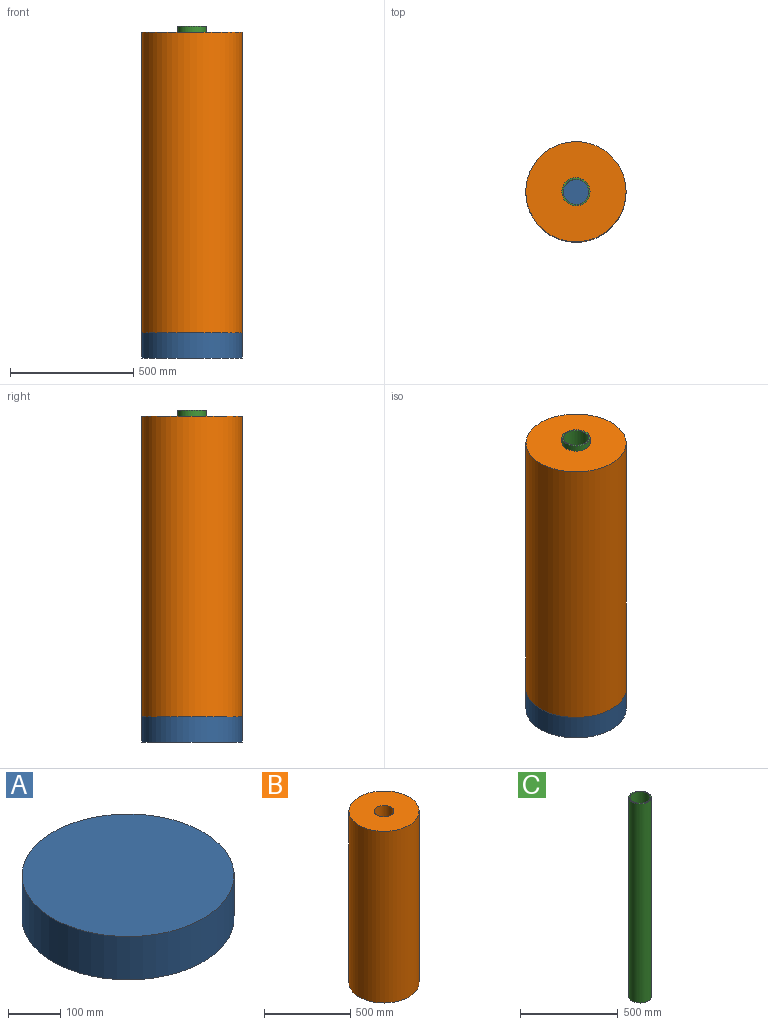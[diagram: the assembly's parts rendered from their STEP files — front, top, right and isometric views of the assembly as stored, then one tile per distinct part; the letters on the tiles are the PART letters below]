
ASSEMBLY  parts=3 mates=3
PART A: 3 faces, bbox 406.4x406.4x101.6 mm
  f0: cylinder r=203.2mm len=406.4mm, axis (0,0,-1), area 129717.1mm2, adj f1,f2
  f1: plane 406.4x406.4mm, normal (0,0,1), area 129717.1mm2, adj f0
  f2: plane 406.4x406.4mm, normal (0,0,-1), area 129717.1mm2, adj f0
PART B: 4 faces, bbox 406.4x406.4x1219.2 mm
  f0: cylinder r=57.15mm len=1219.2mm, axis (0,0,-1), area 437795.3mm2, adj f2,f3
  f1: cylinder r=203.2mm len=1219.2mm, axis (0,0,-1), area 1556605.4mm2, adj f2,f3
  f2: plane 406.4x406.4mm, normal (0,0,1), area 119456.3mm2, adj f0,f1
  f3: plane 406.4x406.4mm, normal (0,0,-1), area 119456.3mm2, adj f0,f1
PART C: 4 faces, bbox 114.3x114.3x1244.6 mm
  f0: cylinder r=51.18mm len=1244.6mm, axis (0,0,-1), area 400238.1mm2, adj f2,f3
  f1: cylinder r=57.15mm len=1244.6mm, axis (0,0,-1), area 446916mm2, adj f2,f3
  f2: plane 114.3x114.3mm, normal (0,0,1), area 2031.4mm2, adj f0,f1
  f3: plane 114.3x114.3mm, normal (0,0,-1), area 2031.4mm2, adj f0,f1
PLACE A t=(-13.41,3.24,-34.34)mm fixed
PLACE B t=(-13.41,3.24,67.26)mm
PLACE C t=(-13.41,3.24,67.26)mm
MATE fastened A.f0 <-> C.f1  axis (0,0,1) through (-13.41,3.24,67.26)mm
MATE fastened C.f1 <-> A.f0  axis (0,0,-1) through (-13.41,3.24,67.26)mm
MATE fastened B.f1 <-> A.f0  axis (0,0,-1) through (-13.41,3.24,67.26)mm
